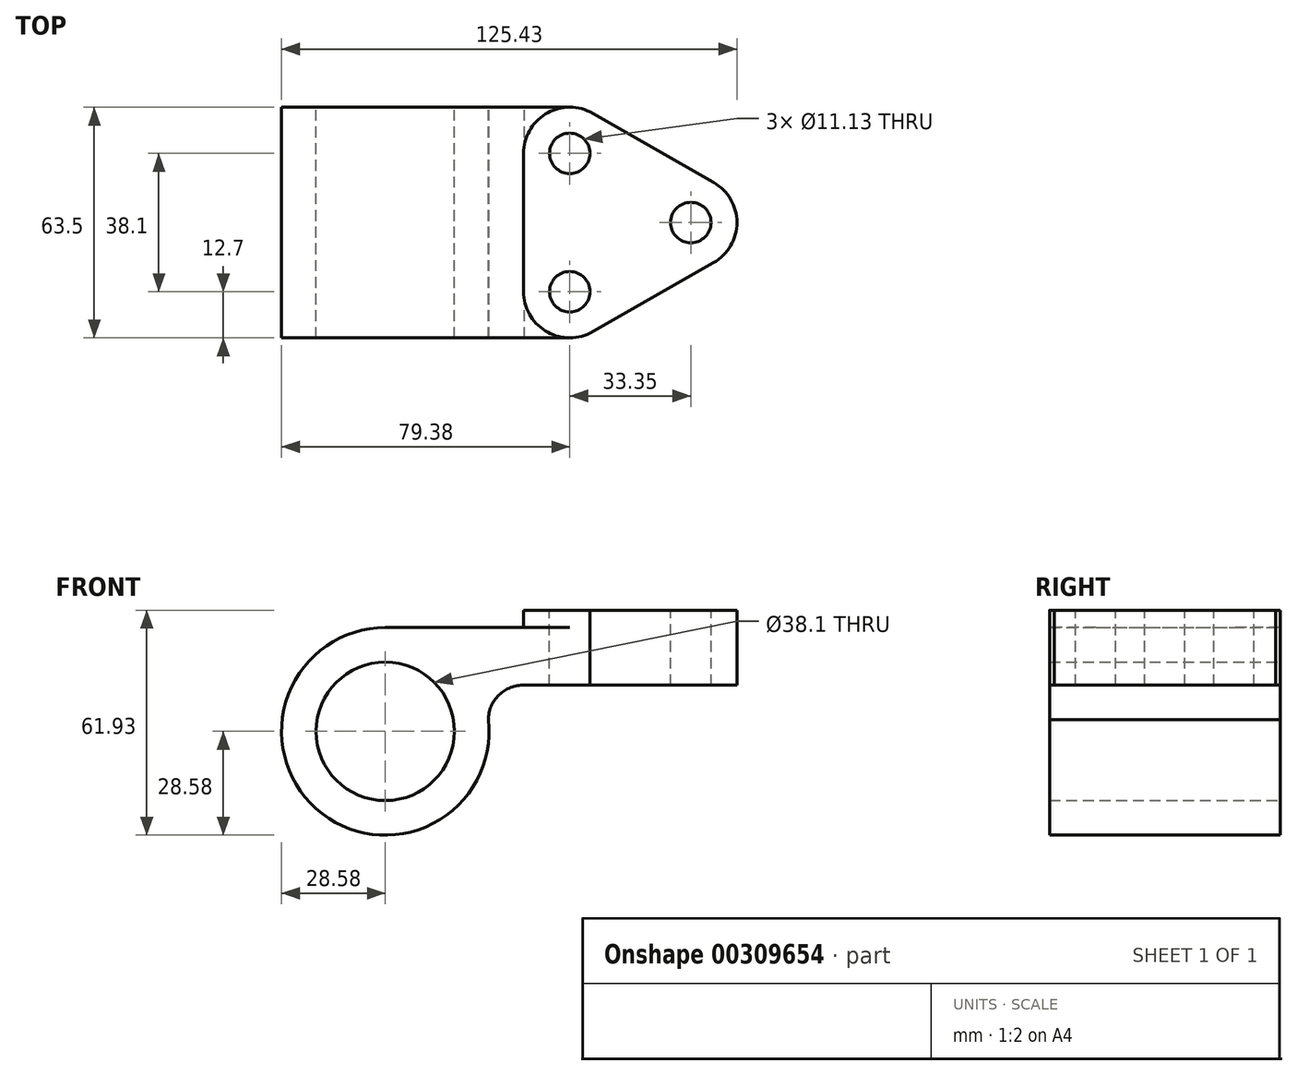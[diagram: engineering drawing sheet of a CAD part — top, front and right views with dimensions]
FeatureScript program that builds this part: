
annotation { "Feature Type Name" : "Feature", "Feature Type Description" : "" }
export const myFeature = defineFeature(function(context is Context, id is Id, definition is map)
    precondition{}
    {
        {
            var Q0;
            Q0=qCreatedBy(makeId("Front.planeOp"),FACE);
            var sketch = newSketch(context, id + "F0", { "sketchPlane" : qUnion([Q0])});
            skCircle(sketch, "E0", {"center": v(0, 0) * mm, "radius": 19.05 * mm});
            skArc(sketch, "E1", {"start": v(0, 28.58) * mm, "mid": v(-19.05, -21.3) * mm, "end": v(28.4, 3.18) * mm});
            skLineSegment(sketch, "E2", {"start": v(0, 28.58) * mm, "end": v(50.8, 28.58) * mm});
            skArc(sketch, "E3", {"start": v(28.4, 3.18) * mm, "mid": v(31.32, 10.05) * mm, "end": v(38.3, 12.7) * mm});
            skLineSegment(sketch, "E4", {"start": v(38.3, 12.7) * mm, "end": v(50.8, 12.7) * mm});
            skLineSegment(sketch, "E5", {"start": v(50.8, 12.7) * mm, "end": v(50.8, 28.58) * mm});
            skSolve(sketch);
        }
        {
            var Q0;
            Q0 = qSketchRegion(id + "F0", true);
            extrude(context, id + "F1", {"entities" : qUnion([Q0]), "depth" : 63.5 * mm});
        }
        {
            var Q0;
            Q0=qCreatedBy(makeId("Top.planeOp"),FACE);
            var sketch = newSketch(context, id + "F2", { "sketchPlane" : qUnion([Q0])});
            skCircle(sketch, "E6", {"center": v(50.8, -12.7) * mm, "radius": 5.56 * mm});
            skCircle(sketch, "E7", {"center": v(50.8, -50.8) * mm, "radius": 5.56 * mm});
            skSolve(sketch);
        }
        {
            var Q0;
            Q0=makeQuery(id+"F1.opExtrude","SWEPT_FACE",FACE,{"disambiguationData":[OSD([sQuery(id+"F0.wireOp",EDGE,"E2")])]});
            var sketch = newSketch(context, id + "F3", { "sketchPlane" : qUnion([Q0])});
            skArc(sketch, "E8", {"start": v(56.33, -1.26) * mm, "mid": v(44.05, -1.94) * mm, "end": v(38.1, -12.7) * mm});
            skArc(sketch, "E9", {"start": v(38.1, -50.8) * mm, "mid": v(44.05, -61.56) * mm, "end": v(56.33, -62.24) * mm});
            skLineSegment(sketch, "E10", {"start": v(56.33, -1.26) * mm, "end": v(90.44, -20.72) * mm});
            skLineSegment(sketch, "E11", {"start": v(56.33, -62.24) * mm, "end": v(90.44, -42.78) * mm});
            skArc(sketch, "E12", {"start": v(90.44, -42.78) * mm, "mid": v(96.85, -31.75) * mm, "end": v(90.44, -20.72) * mm});
            skCircle(sketch, "E13", {"center": v(84.15, -31.75) * mm, "radius": 5.56 * mm});
            skLineSegment(sketch, "E14", {"start": v(38.1, -50.8) * mm, "end": v(38.1, -12.7) * mm});
            skSolve(sketch);
        }
        {
            var Q0;
            Q0 = qSketchRegion(id + "F3", true);
            extrude(context, id + "F4", {"entities" : qUnion([Q0]), "operationType" : NewBodyOperationType.ADD, "oppositeDirection" : true, "depth" : 15.88 * mm, "hasSecondDirection" : true, "secondDirectionOppositeDirection" : false, "secondDirectionDepth" : 4.78 * mm});
        }
        {
            var Q0;
            Q0=makeQuery(id+"F4.opExtrude","CAP_FACE",FACE,{"disambiguationData":[OSD([sQuery(id+"F3.wireOp",EDGE,"E8"),sQuery(id+"F3.wireOp",EDGE,"E9"),sQuery(id+"F3.wireOp",EDGE,"E10"),sQuery(id+"F3.wireOp",EDGE,"E11"),sQuery(id+"F3.wireOp",EDGE,"E12"),sQuery(id+"F3.wireOp",EDGE,"E13"),sQuery(id+"F3.wireOp",EDGE,"E14")])],"isStart":true});
            var sketch = newSketch(context, id + "F5", { "sketchPlane" : qUnion([Q0])});
            skCircle(sketch, "E15", {"center": v(50.8, -12.7) * mm, "radius": 5.56 * mm});
            skCircle(sketch, "E16", {"center": v(50.8, -50.8) * mm, "radius": 5.56 * mm});
            skSolve(sketch);
        }
        {
            var Q0;
            Q0 = qSketchRegion(id + "F5", true);
            extrude(context, id + "F6", {"entities" : qUnion([Q0]), "operationType" : NewBodyOperationType.REMOVE, "endBound" : BoundingType.THROUGH_ALL, "oppositeDirection" : true, "depth" : 25.4 * mm});
        }
    });
